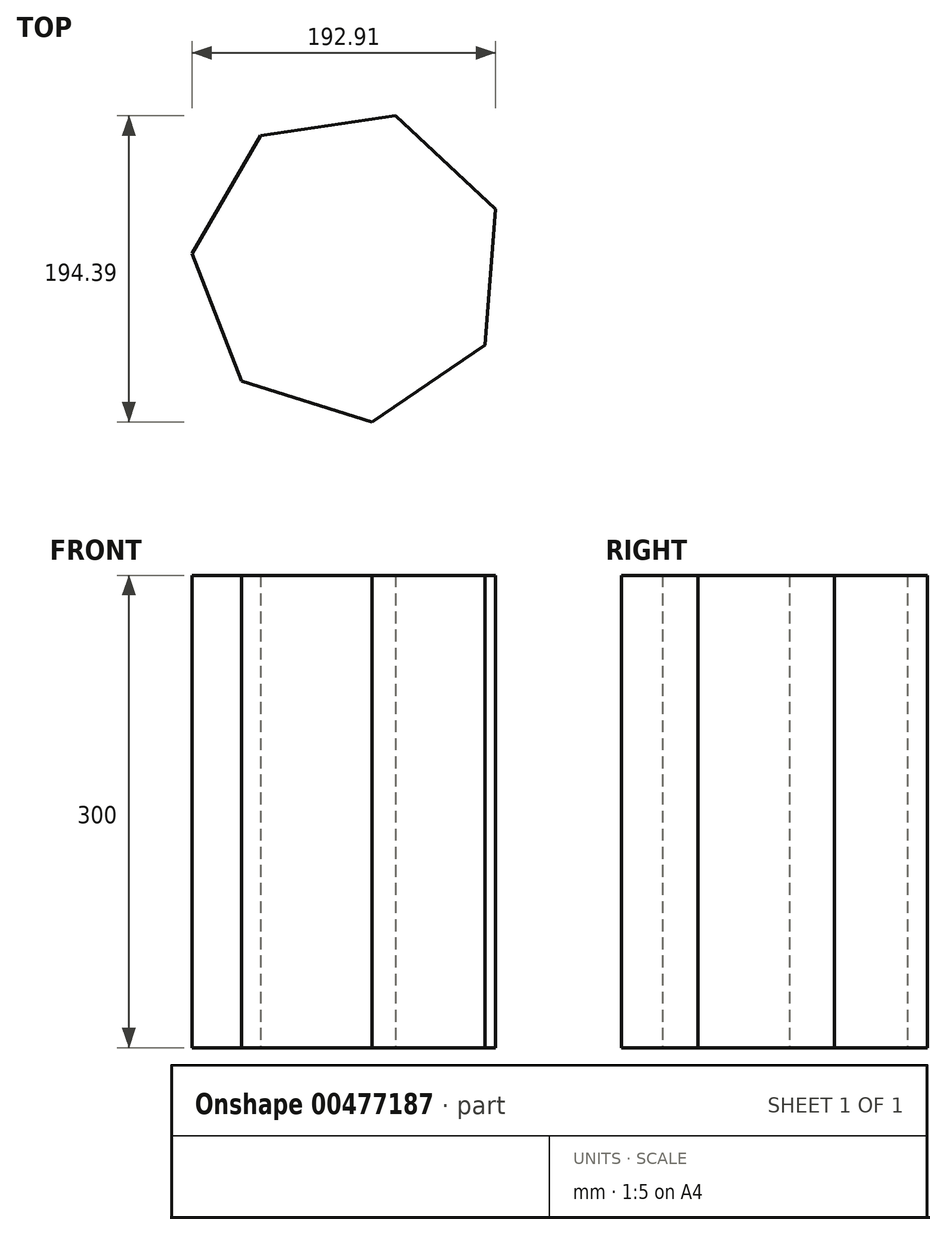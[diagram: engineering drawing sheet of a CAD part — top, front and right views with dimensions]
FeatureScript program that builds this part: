
annotation { "Feature Type Name" : "Feature", "Feature Type Description" : "" }
export const myFeature = defineFeature(function(context is Context, id is Id, definition is map)
    precondition{}
    {
        {
            var Q0;
            Q0=qCreatedBy(makeId("Top.planeOp"),FACE);
            var sketch = newSketch(context, id + "F0", { "sketchPlane" : qUnion([Q0])});
            skCircle(sketch, "E0.cCircle", {"center": v(0, 0) * mm, "radius": 100 * mm, "construction": true});
            skLineSegment(sketch, "E0.0", {"start": v(86.44, -50.28) * mm, "end": v(14.58, -98.93) * mm});
            skLineSegment(sketch, "E0.1", {"start": v(14.58, -98.93) * mm, "end": v(-68.26, -73.08) * mm});
            skLineSegment(sketch, "E0.2", {"start": v(-68.26, -73.08) * mm, "end": v(-99.7, 7.8) * mm});
            skLineSegment(sketch, "E0.3", {"start": v(-99.7, 7.8) * mm, "end": v(-56.06, 82.8) * mm});
            skLineSegment(sketch, "E0.4", {"start": v(-56.06, 82.8) * mm, "end": v(29.8, 95.46) * mm});
            skLineSegment(sketch, "E0.5", {"start": v(29.8, 95.46) * mm, "end": v(93.2, 36.23) * mm});
            skLineSegment(sketch, "E0.6", {"start": v(93.2, 36.23) * mm, "end": v(86.44, -50.28) * mm});
            skSolve(sketch);
        }
        {
            var Q0;
            Q0=makeQuery(id+"F0.imprint","IMPRINT",FACE,{"disambiguationData":[TD([[makeQuery(id+"F0.imprint","IMPRINT",EDGE,{"derivedFrom":sQuery(id+"F0.wireOp",EDGE,"E0.0")}),-1.0]])]});
            extrude(context, id + "F1", {"entities" : qUnion([Q0]), "depth" : 300 * mm});
        }
    });
